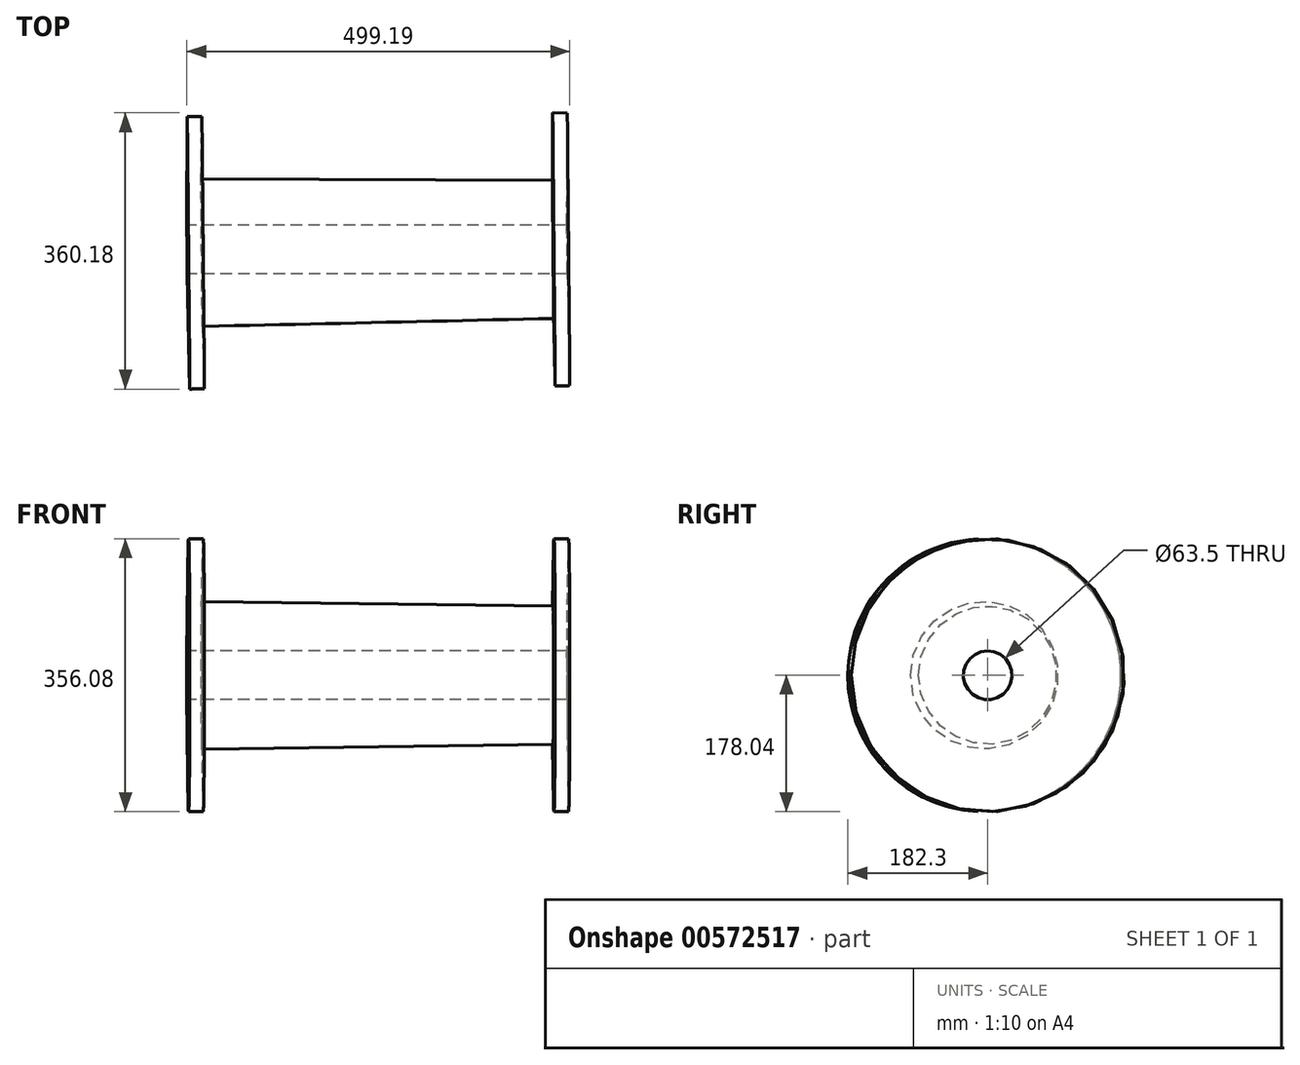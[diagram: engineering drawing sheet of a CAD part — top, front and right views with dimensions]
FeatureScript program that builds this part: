
annotation { "Feature Type Name" : "Feature", "Feature Type Description" : "" }
export const myFeature = defineFeature(function(context is Context, id is Id, definition is map)
    precondition{}
    {
        {
            var Q0;
            Q0=qCreatedBy(makeId("Top.planeOp"),FACE);
            var sketch = newSketch(context, id + "F0", { "sketchPlane" : qUnion([Q0])});
            skLineSegment(sketch, "E0", {"start": v(-288.14, -4.55) * mm, "end": v(-284.11, -182.3) * mm});
            skLineSegment(sketch, "E1", {"start": v(-284.11, -182.3) * mm, "end": v(-265.07, -181.87) * mm});
            skLineSegment(sketch, "E2", {"start": v(192.17, -178.19) * mm, "end": v(211.21, -177.75) * mm});
            skLineSegment(sketch, "E3", {"start": v(211.21, -177.75) * mm, "end": v(207.19, 0) * mm});
            skLineSegment(sketch, "E4", {"start": v(-144.1, 0) * mm, "end": v(264.8, 0) * mm, "construction": true});
            skLineSegment(sketch, "E5", {"start": v(192.17, -178.19) * mm, "end": v(190.18, -90.23) * mm});
            skLineSegment(sketch, "E6", {"start": v(190.18, -90.23) * mm, "end": v(-267.9, -100.6) * mm});
            skLineSegment(sketch, "E7", {"start": v(-265.07, -181.87) * mm, "end": v(-267.9, -100.6) * mm});
            skLineSegment(sketch, "E8", {"start": v(-288.14, -4.55) * mm, "end": v(207.19, 0) * mm});
            skSolve(sketch);
        }
        {
            var Q0;
            Q0=makeQuery(id+"F0.imprint","IMPRINT",FACE,{"disambiguationData":[TD([[makeQuery(id+"F0.imprint","IMPRINT",EDGE,{"derivedFrom":sQuery(id+"F0.wireOp",EDGE,"E0")}),1.0]])]});
            var Q1;
            Q1=sQuery(id+"F0.wireOp",EDGE,"E8");
            revolve(context, id + "F1", {"entities" : qUnion([Q0]), "axis" : qUnion([Q1]), "revolveType" : RevolveType.FULL});
        }
        {
            var Q0;
            Q0=qCreatedBy(makeId("Right.planeOp"),FACE);
            var sketch = newSketch(context, id + "F2", { "sketchPlane" : qUnion([Q0])});
            skCircle(sketch, "E9", {"center": v(0, 0) * mm, "radius": 31.75 * mm});
            skSolve(sketch);
        }
        {
            var Q0;
            Q0 = qSketchRegion(id + "F2", true);
            extrude(context, id + "F3", {"entities" : qUnion([Q0]), "operationType" : NewBodyOperationType.REMOVE, "endBound" : BoundingType.THROUGH_ALL, "depth" : 25.4 * mm, "offsetDistance" : 25.4 * mm, "hasSecondDirection" : true, "secondDirectionBound" : SecondDirectionBoundingType.THROUGH_ALL, "secondDirectionOppositeDirection" : true, "secondDirectionDepth" : 25.4 * mm});
        }
    });
